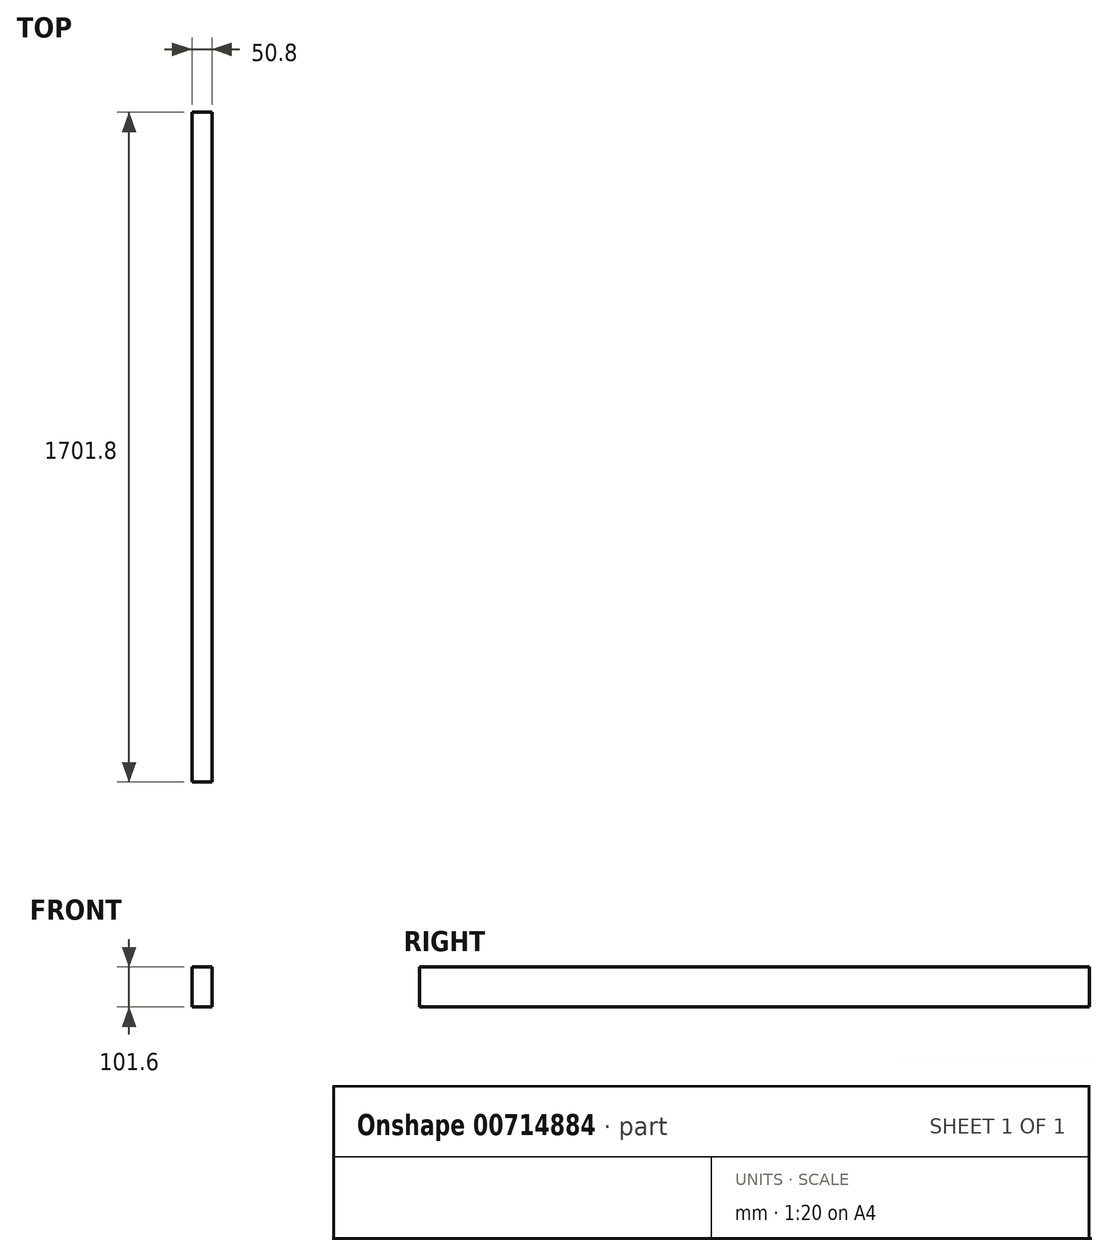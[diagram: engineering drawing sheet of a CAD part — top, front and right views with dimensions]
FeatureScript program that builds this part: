
annotation { "Feature Type Name" : "Feature", "Feature Type Description" : "" }
export const myFeature = defineFeature(function(context is Context, id is Id, definition is map)
    precondition{}
    {
        {
            var Q0;
            Q0=qCreatedBy(makeId("Right.planeOp"),FACE);
            var sketch = newSketch(context, id + "F0", { "sketchPlane" : qUnion([Q0])});
            skLineSegment(sketch, "E0.bottom", {"start": v(1701.8, 101.6) * mm, "end": v(0, 101.6) * mm});
            skLineSegment(sketch, "E0.top", {"start": v(1701.8, 0) * mm, "end": v(0, 0) * mm});
            skLineSegment(sketch, "E0.left", {"start": v(1701.8, 101.6) * mm, "end": v(1701.8, 0) * mm});
            skLineSegment(sketch, "E0.right", {"start": v(0, 101.6) * mm, "end": v(0, 0) * mm});
            skSolve(sketch);
        }
        {
            var Q0;
            Q0=makeQuery(id+"F0.imprint","IMPRINT",FACE,{"disambiguationData":[TD([[makeQuery(id+"F0.imprint","IMPRINT",EDGE,{"derivedFrom":sQuery(id+"F0.wireOp",EDGE,"E0.bottom")}),1.0]])]});
            extrude(context, id + "F1", {"entities" : qUnion([Q0]), "depth" : 50.8 * mm, "offsetDistance" : 25.4 * mm});
        }
    });
